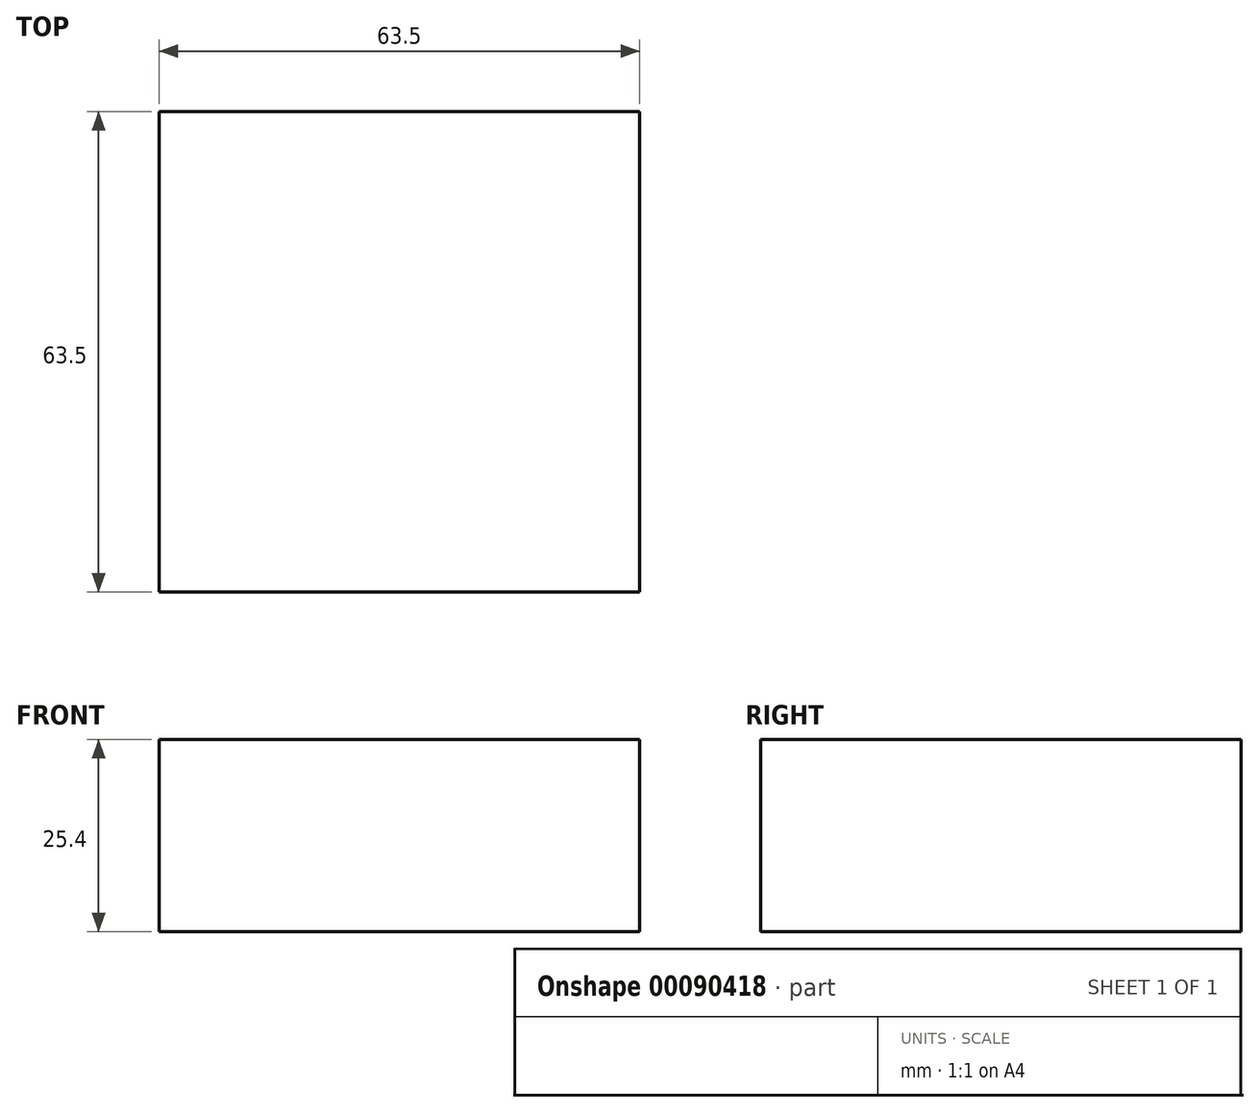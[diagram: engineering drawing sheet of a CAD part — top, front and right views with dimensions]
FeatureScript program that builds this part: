
annotation { "Feature Type Name" : "Feature", "Feature Type Description" : "" }
export const myFeature = defineFeature(function(context is Context, id is Id, definition is map)
    precondition{}
    {
        {
            var Q0;
            Q0=qCreatedBy(makeId("Top.planeOp"),FACE);
            var sketch = newSketch(context, id + "F0", { "sketchPlane" : qUnion([Q0])});
            skLineSegment(sketch, "E0.bottom", {"start": v(-32.43, 32.24) * mm, "end": v(31.07, 32.24) * mm});
            skLineSegment(sketch, "E0.top", {"start": v(-32.43, -31.26) * mm, "end": v(31.07, -31.26) * mm});
            skLineSegment(sketch, "E0.left", {"start": v(-32.43, 32.24) * mm, "end": v(-32.43, -31.26) * mm});
            skLineSegment(sketch, "E0.right", {"start": v(31.07, 32.24) * mm, "end": v(31.07, -31.26) * mm});
            skSolve(sketch);
        }
        {
            var Q0;
            Q0 = qSketchRegion(id + "F0", true);
            extrude(context, id + "F1", {"entities" : qUnion([Q0]), "depth" : 25.4 * mm});
        }
    });
